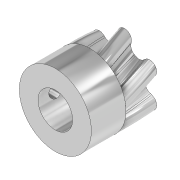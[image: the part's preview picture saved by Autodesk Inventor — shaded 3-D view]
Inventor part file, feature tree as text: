
AUTODESK INVENTOR PART (.ipt)
format: ipt  version: 2020 (Build 240168000, 168)  size: 369,152 bytes
history: native  units: in
note: dims shown in document units (in); Inventor stores cm internally (conversion verified against a paired STEP export)
features: sketch x5, extrude x2, sweep x1, other x1, projected_geometry x1
ambient origin geometry x8: Origin, YZ Plane, XZ Plane, XY Plane, X Axis, Y Axis, Z Axis, Center Point
bodies: Solid1 (feature_tree)
feature tree (10):
  sweep  "Sweep1"
  sketch  "3D Sketch2"
  extrude  "Extrusion1"  Depth=0.0787in
  extrude  "Extrusion2"  Depth=0.1969in
  sketch  "Sketch1"  dims[d0=0.1969in d1=0.4094in]
  sketch  "3D Sketch1"
  other  "Helical Curve1"
  sketch  "Sketch2"  dims[d2=0.0866in d3=0.0787in]
  projected_geometry  "Projected Loop1"
  sketch  "Sketch3"  dims[d4=0.0787in d5=0.0787in d6=2.3622in d8=360.0deg d10=0.1969in d11=0.0236in d12=0.236in d13=0.0in d14=0.0in d15=0.0in d16=0.1969in d17=0.0in d18=0.0748in d19=0.205in d20=0.0in]
